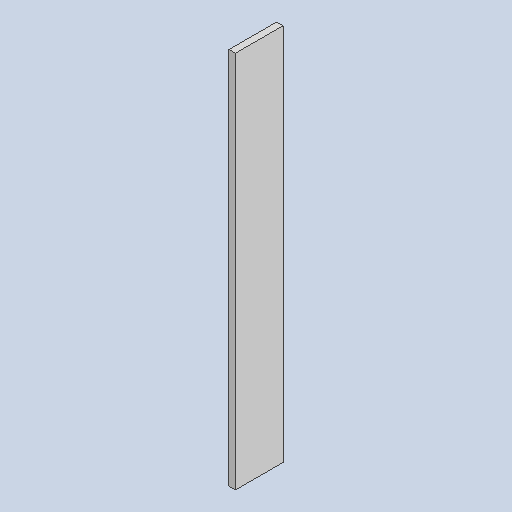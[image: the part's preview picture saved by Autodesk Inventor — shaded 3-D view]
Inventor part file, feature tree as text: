
AUTODESK INVENTOR PART (.ipt)
format: ipt  version: 2025 (Build 290162010, 162A)  size: 91,136 bytes
history: native  units: mm
features: extrude x1, sketch x1
ambient origin geometry x8: Origin, YZ Plane, XZ Plane, XY Plane, X Axis, Y Axis, Z Axis, Center Point
bodies: Solid1 (feature_tree)
feature tree (2):
  extrude  "Extrusion1"  Depth=74.0mm
  sketch  "Sketch1"  dims[d0=513.0mm d1=260.0mm d2=635.0mm d6=5.0mm d7=74.0mm d8=0.0mm]
